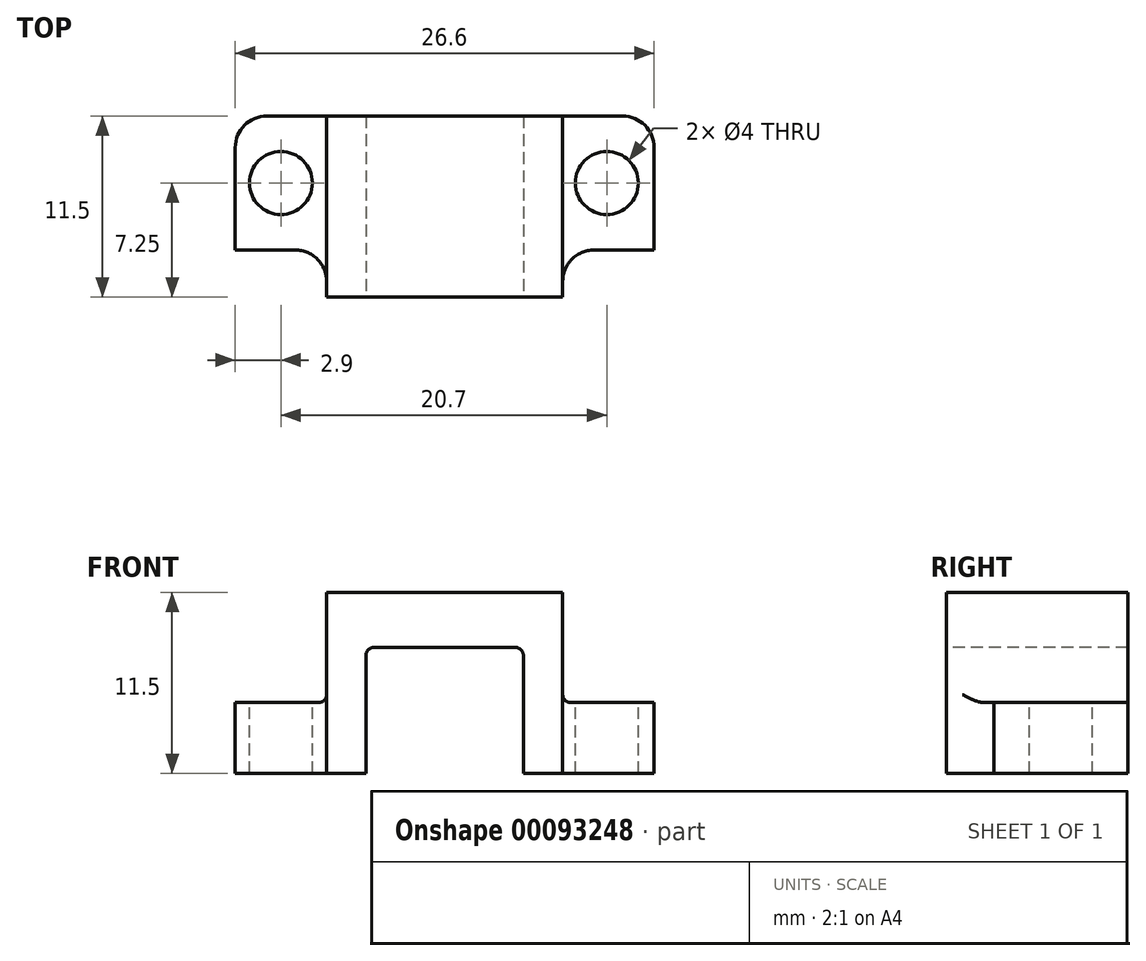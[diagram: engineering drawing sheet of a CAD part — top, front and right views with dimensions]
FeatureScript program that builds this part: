
annotation { "Feature Type Name" : "Feature", "Feature Type Description" : "" }
export const myFeature = defineFeature(function(context is Context, id is Id, definition is map)
    precondition{}
    {
        {
            var Q0;
            Q0=qCreatedBy(makeId("Top.planeOp"),FACE);
            var sketch = newSketch(context, id + "F0", { "sketchPlane" : qUnion([Q0])});
            skLineSegment(sketch, "E0.bottom", {"start": v(-13.3, 5.75) * mm, "end": v(13.3, 5.75) * mm});
            skLineSegment(sketch, "E0.top", {"start": v(-13.3, -5.75) * mm, "end": v(13.3, -5.75) * mm});
            skLineSegment(sketch, "E0.left", {"start": v(-13.3, 5.75) * mm, "end": v(-13.3, -5.75) * mm});
            skLineSegment(sketch, "E0.right", {"start": v(13.3, 5.75) * mm, "end": v(13.3, -5.75) * mm});
            skPoint(sketch, "E1", {"position": v(0, 5.75) * mm});
            skPoint(sketch, "E2", {"position": v(13.3, 0) * mm});
            skSolve(sketch);
        }
        {
            var Q0;
            Q0 = qSketchRegion(id + "F0", true);
            extrude(context, id + "F1", {"entities" : qUnion([Q0]), "depth" : 11.5 * mm});
        }
        {
            var Q0;
            Q0=makeQuery(id+"F1.opExtrude","SWEPT_FACE",FACE,{"disambiguationData":[OSD([sQuery(id+"F0.wireOp",EDGE,"E0.top")])]});
            var sketch = newSketch(context, id + "F2", { "sketchPlane" : qUnion([Q0])});
            skLineSegment(sketch, "E3.bottom", {"start": v(-13.3, 11.5) * mm, "end": v(-7.5, 11.5) * mm});
            skLineSegment(sketch, "E3.top", {"start": v(-13.3, 4.5) * mm, "end": v(-7.5, 4.5) * mm});
            skLineSegment(sketch, "E3.left", {"start": v(-13.3, 11.5) * mm, "end": v(-13.3, 4.5) * mm});
            skLineSegment(sketch, "E3.right", {"start": v(-7.5, 11.5) * mm, "end": v(-7.5, 4.5) * mm});
            skLineSegment(sketch, "E4.bottom", {"start": v(13.3, 11.5) * mm, "end": v(7.5, 11.5) * mm});
            skLineSegment(sketch, "E4.top", {"start": v(13.3, 4.5) * mm, "end": v(7.5, 4.5) * mm});
            skLineSegment(sketch, "E4.left", {"start": v(13.3, 11.5) * mm, "end": v(13.3, 4.5) * mm});
            skLineSegment(sketch, "E4.right", {"start": v(7.5, 11.5) * mm, "end": v(7.5, 4.5) * mm});
            skLineSegment(sketch, "E5.bottom", {"start": v(-5, 0) * mm, "end": v(5, 0) * mm});
            skLineSegment(sketch, "E5.top", {"start": v(-5, 8) * mm, "end": v(5, 8) * mm});
            skLineSegment(sketch, "E5.left", {"start": v(-5, 0) * mm, "end": v(-5, 8) * mm});
            skLineSegment(sketch, "E5.right", {"start": v(5, 0) * mm, "end": v(5, 8) * mm});
            skPoint(sketch, "E6", {"position": v(0, 8) * mm});
            skSolve(sketch);
        }
        {
            var Q0;
            Q0 = qSketchRegion(id + "F2", true);
            extrude(context, id + "F3", {"entities" : qUnion([Q0]), "operationType" : NewBodyOperationType.REMOVE, "endBound" : BoundingType.THROUGH_ALL, "oppositeDirection" : true, "depth" : 25 * mm});
        }
        {
            var Q0;
            Q0=makeQuery(id+"F3.boolean.opBoolean","COPY",FACE,{"derivedFrom":makeQuery(id+"F3.opExtrude","SWEPT_FACE",FACE,{"disambiguationData":[OSD([sQuery(id+"F2.wireOp",EDGE,"E3.top")])]})});
            var sketch = newSketch(context, id + "F4", { "sketchPlane" : qUnion([Q0])});
            skLineSegment(sketch, "E7.bottom", {"start": v(-13.3, -5.75) * mm, "end": v(-7.5, -5.75) * mm});
            skLineSegment(sketch, "E7.top", {"start": v(-13.3, -2.75) * mm, "end": v(-7.5, -2.75) * mm});
            skLineSegment(sketch, "E7.left", {"start": v(-13.3, -5.75) * mm, "end": v(-13.3, -2.75) * mm});
            skLineSegment(sketch, "E7.right", {"start": v(-7.5, -5.75) * mm, "end": v(-7.5, -2.75) * mm});
            skCircle(sketch, "E8", {"center": v(-10.4, 1.5) * mm, "radius": 2 * mm});
            skPoint(sketch, "E8.centerSnap0", {"position": v(-10.4, 5.75) * mm});
            skSolve(sketch);
        }
        {
            var Q0;
            Q0 = qSketchRegion(id + "F4", true);
            extrude(context, id + "F5", {"entities" : qUnion([Q0]), "operationType" : NewBodyOperationType.REMOVE, "endBound" : BoundingType.THROUGH_ALL, "oppositeDirection" : true, "depth" : 25 * mm});
        }
        {
            var Q0;
            Q0=makeQuery(id+"F3.boolean.opBoolean","COPY",FACE,{"derivedFrom":makeQuery(id+"F3.opExtrude","SWEPT_FACE",FACE,{"disambiguationData":[OSD([sQuery(id+"F2.wireOp",EDGE,"E4.top")])]})});
            var sketch = newSketch(context, id + "F6", { "sketchPlane" : qUnion([Q0])});
            skLineSegment(sketch, "E9.bottom", {"start": v(13.3, -5.75) * mm, "end": v(7.5, -5.75) * mm});
            skLineSegment(sketch, "E9.top", {"start": v(13.3, -2.75) * mm, "end": v(7.5, -2.75) * mm});
            skLineSegment(sketch, "E9.left", {"start": v(13.3, -5.75) * mm, "end": v(13.3, -2.75) * mm});
            skLineSegment(sketch, "E9.right", {"start": v(7.5, -5.75) * mm, "end": v(7.5, -2.75) * mm});
            skCircle(sketch, "E10", {"center": v(10.3, 1.5) * mm, "radius": 2 * mm});
            skPoint(sketch, "E11", {"position": v(10.4, 5.75) * mm});
            skSolve(sketch);
        }
        {
            var Q0;
            Q0 = qSketchRegion(id + "F6", true);
            extrude(context, id + "F7", {"entities" : qUnion([Q0]), "operationType" : NewBodyOperationType.REMOVE, "endBound" : BoundingType.THROUGH_ALL, "oppositeDirection" : true, "depth" : 25 * mm});
        }
        {
            var Q0;
            Q0=makeQuery(id+"F3.boolean.opBoolean","COPY",EDGE,{"derivedFrom":makeQuery(id+"F3.opExtrude","SWEPT_EDGE",EDGE,{"disambiguationData":[OSD([sQuery(id+"F0.wireOp",EDGE,"E0.top"),sQuery(id+"F2.wireOp",EDGE,"E3.bottom"),sQuery(id+"F2.wireOp",EDGE,"E3.right")])]})});
            var Q1;
            Q1=makeQuery(id+"F3.boolean.opBoolean","COPY",EDGE,{"derivedFrom":makeQuery(id+"F3.opExtrude","SWEPT_EDGE",EDGE,{"disambiguationData":[OSD([sQuery(id+"F0.wireOp",EDGE,"E0.top"),sQuery(id+"F2.wireOp",EDGE,"E4.bottom"),sQuery(id+"F2.wireOp",EDGE,"E4.right")])]})});
            var Q2;
            Q2=makeQuery(id+"F5.boolean.opBoolean","COPY",EDGE,{"derivedFrom":makeQuery(id+"F5.opExtrude","SWEPT_EDGE",EDGE,{"disambiguationData":[OSD([sQuery(id+"F0.wireOp",EDGE,"E0.top"),sQuery(id+"F0.wireOp",EDGE,"E0.left"),sQuery(id+"F2.wireOp",EDGE,"E3.top"),sQuery(id+"F2.wireOp",EDGE,"E3.left"),sQuery(id+"F4.wireOp",EDGE,"E7.top"),sQuery(id+"F4.wireOp",EDGE,"E7.left")])]})});
            var Q3;
            Q3=makeQuery(id+"F1.opExtrude","SWEPT_EDGE",EDGE,{"disambiguationData":[OSD([sQuery(id+"F0.wireOp",EDGE,"E0.bottom"),sQuery(id+"F0.wireOp",EDGE,"E0.left")])]});
            var Q4;
            Q4=makeQuery(id+"F5.boolean.opBoolean","COPY",EDGE,{"derivedFrom":makeQuery(id+"F5.opExtrude","SWEPT_EDGE",EDGE,{"disambiguationData":[OSD([sQuery(id+"F2.wireOp",EDGE,"E3.top"),sQuery(id+"F2.wireOp",EDGE,"E3.right"),sQuery(id+"F4.wireOp",EDGE,"E7.top"),sQuery(id+"F4.wireOp",EDGE,"E7.right")])]})});
            var Q5;
            Q5=makeQuery(id+"F1.opExtrude","SWEPT_EDGE",EDGE,{"disambiguationData":[OSD([sQuery(id+"F0.wireOp",EDGE,"E0.bottom"),sQuery(id+"F0.wireOp",EDGE,"E0.right")])]});
            var Q6;
            Q6=makeQuery(id+"F7.boolean.opBoolean","COPY",EDGE,{"derivedFrom":makeQuery(id+"F7.opExtrude","SWEPT_EDGE",EDGE,{"disambiguationData":[OSD([sQuery(id+"F0.wireOp",EDGE,"E0.top"),sQuery(id+"F0.wireOp",EDGE,"E0.right"),sQuery(id+"F2.wireOp",EDGE,"E4.top"),sQuery(id+"F2.wireOp",EDGE,"E4.left"),sQuery(id+"F6.wireOp",EDGE,"E9.top"),sQuery(id+"F6.wireOp",EDGE,"E9.left")])]})});
            var Q7;
            Q7=makeQuery(id+"F7.boolean.opBoolean","COPY",EDGE,{"derivedFrom":makeQuery(id+"F7.opExtrude","SWEPT_EDGE",EDGE,{"disambiguationData":[OSD([sQuery(id+"F2.wireOp",EDGE,"E4.top"),sQuery(id+"F2.wireOp",EDGE,"E4.right"),sQuery(id+"F6.wireOp",EDGE,"E9.top"),sQuery(id+"F6.wireOp",EDGE,"E9.right")])]})});
            fillet(context, id + "F8", {"entities" : qUnion([Q0, Q1, Q2, Q3, Q4, Q5, Q6, Q7]), "radius" : 2 * mm, "tangentPropagation" : true, "allowEdgeOverflow" : false});
        }
        {
            var Q0;
            Q0=makeQuery(id+"F3.boolean.opBoolean","COPY",EDGE,{"derivedFrom":makeQuery(id+"F3.opExtrude","SWEPT_EDGE",EDGE,{"disambiguationData":[OSD([sQuery(id+"F2.wireOp",EDGE,"E3.top"),sQuery(id+"F2.wireOp",EDGE,"E3.right")])]})});
            var Q1;
            Q1=makeQuery(id+"F3.boolean.opBoolean","COPY",EDGE,{"derivedFrom":makeQuery(id+"F3.opExtrude","SWEPT_EDGE",EDGE,{"disambiguationData":[OSD([sQuery(id+"F2.wireOp",EDGE,"E4.top"),sQuery(id+"F2.wireOp",EDGE,"E4.right")])]})});
            var Q2;
            Q2=makeQuery(id+"F3.boolean.opBoolean","COPY",EDGE,{"derivedFrom":makeQuery(id+"F3.opExtrude","SWEPT_EDGE",EDGE,{"disambiguationData":[OSD([sQuery(id+"F2.wireOp",EDGE,"E5.top"),sQuery(id+"F2.wireOp",EDGE,"E5.left")])]})});
            var Q3;
            Q3=makeQuery(id+"F3.boolean.opBoolean","COPY",EDGE,{"derivedFrom":makeQuery(id+"F3.opExtrude","SWEPT_EDGE",EDGE,{"disambiguationData":[OSD([sQuery(id+"F2.wireOp",EDGE,"E5.top"),sQuery(id+"F2.wireOp",EDGE,"E5.right")])]})});
            fillet(context, id + "F9", {"entities" : qUnion([Q0, Q1, Q2, Q3]), "radius" : 0.5 * mm, "tangentPropagation" : true, "allowEdgeOverflow" : false});
        }
    });
